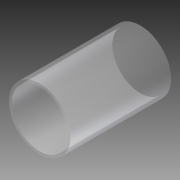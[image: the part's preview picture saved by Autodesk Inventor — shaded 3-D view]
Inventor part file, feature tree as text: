
AUTODESK INVENTOR PART (.ipt)
format: ipt  version: 2015 (Build 190159000, 159)  size: 83,968 bytes
history: native  units: mm
features: extrude x1, sketch x1
ambient origin geometry x8: Origin, YZ Plane, XZ Plane, XY Plane, X Axis, Y Axis, Z Axis, Center Point
bodies: Solid1 (feature_tree)
feature tree (2):
  extrude  "Extrusion1"  Depth=180.0mm
  sketch  "Sketch1"  dims[d0=110.0mm d1=100.0mm d2=180.0mm d3=0.0mm]
